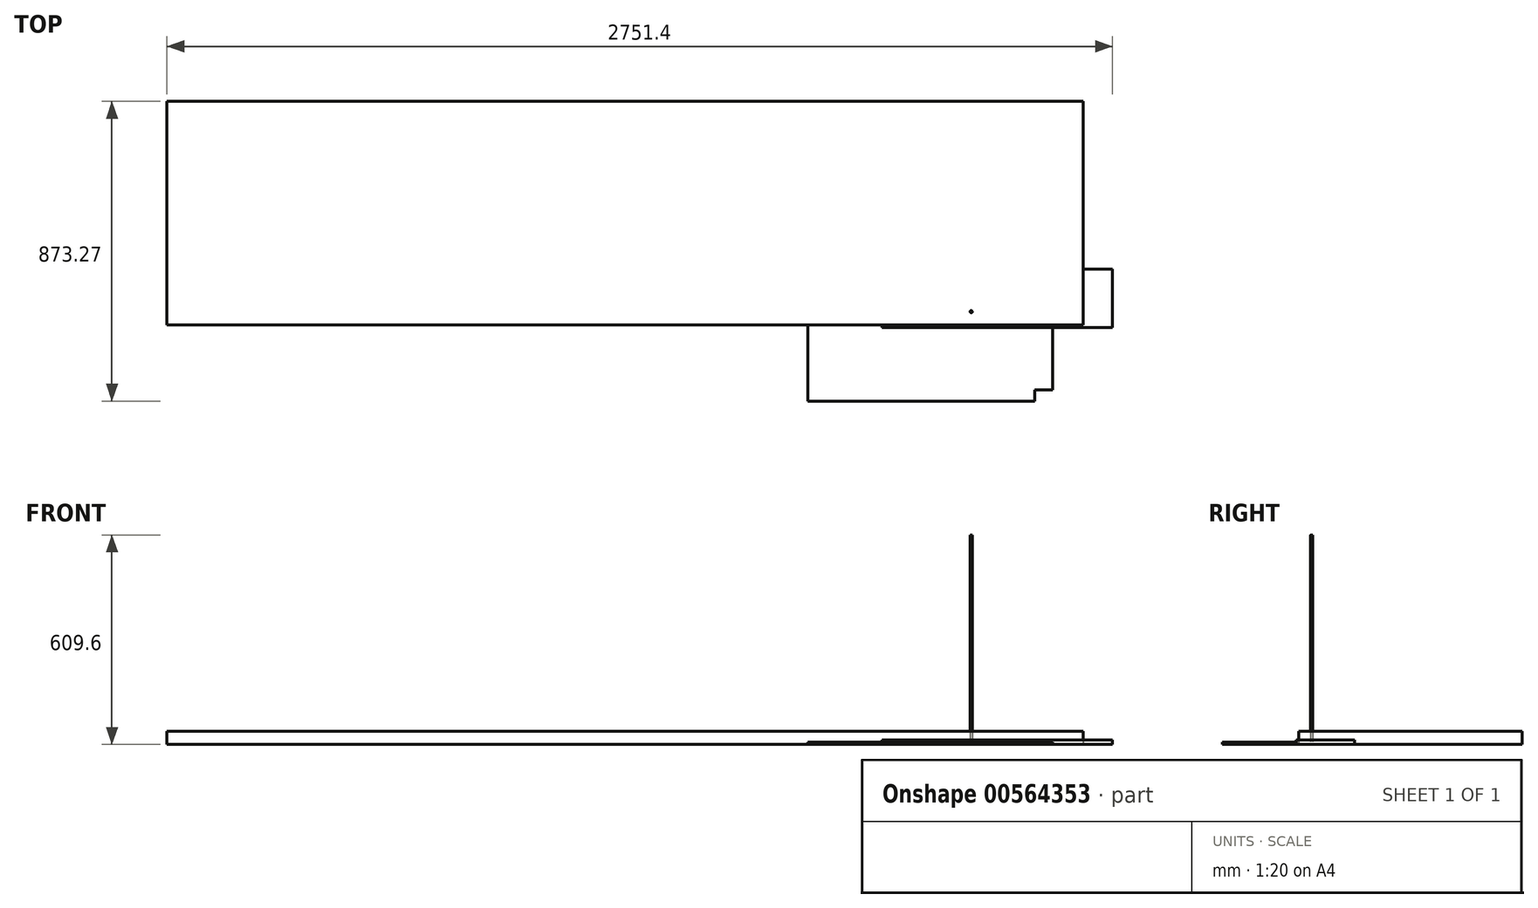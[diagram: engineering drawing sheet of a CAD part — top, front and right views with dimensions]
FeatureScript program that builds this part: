
annotation { "Feature Type Name" : "Feature", "Feature Type Description" : "" }
export const myFeature = defineFeature(function(context is Context, id is Id, definition is map)
    precondition{}
    {
        {
            var Q0;
            Q0=qCreatedBy(makeId("Top.planeOp"),FACE);
            var sketch = newSketch(context, id + "F0", { "sketchPlane" : qUnion([Q0])});
            skLineSegment(sketch, "E0.bottom", {"start": v(-2407.4, 611.97) * mm, "end": v(81.8, 611.97) * mm});
            skLineSegment(sketch, "E0.top", {"start": v(-2407.4, -38.9) * mm, "end": v(81.8, -38.9) * mm});
            skLineSegment(sketch, "E0.left", {"start": v(-2407.4, 611.97) * mm, "end": v(-2407.4, -38.9) * mm});
            skLineSegment(sketch, "E0.right", {"start": v(81.8, 611.97) * mm, "end": v(81.8, -38.9) * mm});
            skSolve(sketch);
        }
        {
            var Q0;
            Q0=makeQuery(id+"F0.imprint","IMPRINT",FACE,{"disambiguationData":[TD([[makeQuery(id+"F0.imprint","IMPRINT",EDGE,{"derivedFrom":sQuery(id+"F0.wireOp",EDGE,"E0.bottom")}),-1.0]])]});
            extrude(context, id + "F1", {"entities" : qUnion([Q0]), "depth" : 38.1 * mm, "offsetDistance" : 25.4 * mm});
        }
        {
            var Q0;
            Q0=qCreatedBy(makeId("Top.planeOp"),FACE);
            var sketch = newSketch(context, id + "F2", { "sketchPlane" : qUnion([Q0])});
            skLineSegment(sketch, "E1.bottom", {"start": v(-331.11, 48.4) * mm, "end": v(100.69, 48.4) * mm});
            skLineSegment(sketch, "E1.top", {"start": v(-331.11, -15.1) * mm, "end": v(100.69, -15.1) * mm});
            skLineSegment(sketch, "E1.left", {"start": v(-331.11, 48.4) * mm, "end": v(-331.11, -15.1) * mm});
            skLineSegment(sketch, "E1.right", {"start": v(100.69, 48.4) * mm, "end": v(100.69, -15.1) * mm});
            skSolve(sketch);
        }
        {
            var Q0;
            Q0=makeQuery(id+"F2.imprint","IMPRINT",FACE,{"disambiguationData":[TD([[makeQuery(id+"F2.imprint","IMPRINT",EDGE,{"derivedFrom":sQuery(id+"F2.wireOp",EDGE,"E1.bottom")}),-1.0]])]});
            extrude(context, id + "F3", {"entities" : qUnion([Q0]), "depth" : 12.7 * mm, "offsetDistance" : 25.4 * mm});
        }
        {
            var Q0;
            Q0=qCreatedBy(makeId("Top.planeOp"),FACE);
            var sketch = newSketch(context, id + "F4", { "sketchPlane" : qUnion([Q0])});
            skLineSegment(sketch, "E2.bottom", {"start": v(-326.55, 123.75) * mm, "end": v(166.2, 123.75) * mm});
            skLineSegment(sketch, "E2.top", {"start": v(-326.55, -46.43) * mm, "end": v(166.2, -46.43) * mm});
            skLineSegment(sketch, "E2.left", {"start": v(-326.55, 123.75) * mm, "end": v(-326.55, -46.43) * mm});
            skLineSegment(sketch, "E2.right", {"start": v(166.2, 123.75) * mm, "end": v(166.2, -46.43) * mm});
            skSolve(sketch);
        }
        {
            var Q0;
            Q0=makeQuery(id+"F4.imprint","IMPRINT",FACE,{"disambiguationData":[TD([[makeQuery(id+"F4.imprint","IMPRINT",EDGE,{"derivedFrom":sQuery(id+"F4.wireOp",EDGE,"E2.bottom")}),-1.0]])]});
            extrude(context, id + "F5", {"entities" : qUnion([Q0]), "depth" : 12.7 * mm, "offsetDistance" : 25.4 * mm});
        }
        {
            var Q0;
            Q0=qCreatedBy(makeId("Top.planeOp"),FACE);
            var sketch = newSketch(context, id + "F6", { "sketchPlane" : qUnion([Q0])});
            skLineSegment(sketch, "E3.bottom", {"start": v(-414.47, 393.37) * mm, "end": v(169.73, 393.37) * mm});
            skLineSegment(sketch, "E3.top", {"start": v(-414.47, -51.13) * mm, "end": v(169.73, -51.13) * mm});
            skLineSegment(sketch, "E3.left", {"start": v(-414.47, 393.37) * mm, "end": v(-414.47, -51.13) * mm});
            skLineSegment(sketch, "E3.right", {"start": v(169.73, 393.37) * mm, "end": v(169.73, -51.13) * mm});
            skSolve(sketch);
        }
        {
            var Q0;
            Q0=makeQuery(id+"F6.imprint","IMPRINT",FACE,{"disambiguationData":[TD([[makeQuery(id+"F6.imprint","IMPRINT",EDGE,{"derivedFrom":sQuery(id+"F6.wireOp",EDGE,"E3.bottom")}),-1.0]])]});
            extrude(context, id + "F7", {"entities" : qUnion([Q0]), "depth" : 6.35 * mm, "offsetDistance" : 25.4 * mm});
        }
        {
            var Q0;
            Q0=qCreatedBy(makeId("Top.planeOp"),FACE);
            var sketch = newSketch(context, id + "F8", { "sketchPlane" : qUnion([Q0])});
            skLineSegment(sketch, "E4.bottom", {"start": v(-542.59, 361) * mm, "end": v(117.81, 361) * mm});
            skLineSegment(sketch, "E4.top", {"start": v(-542.59, -83.5) * mm, "end": v(117.81, -83.5) * mm});
            skLineSegment(sketch, "E4.left", {"start": v(-542.59, 361) * mm, "end": v(-542.59, -83.5) * mm});
            skLineSegment(sketch, "E4.right", {"start": v(117.81, 361) * mm, "end": v(117.81, -83.5) * mm});
            skSolve(sketch);
        }
        {
            var Q0;
            Q0=makeQuery(id+"F8.imprint","IMPRINT",FACE,{"disambiguationData":[TD([[makeQuery(id+"F8.imprint","IMPRINT",EDGE,{"derivedFrom":sQuery(id+"F8.wireOp",EDGE,"E4.bottom")}),-1.0]])]});
            extrude(context, id + "F9", {"entities" : qUnion([Q0]), "depth" : 6.35 * mm, "offsetDistance" : 25.4 * mm});
        }
        {
            var Q0;
            Q0=qCreatedBy(makeId("Top.planeOp"),FACE);
            var sketch = newSketch(context, id + "F10", { "sketchPlane" : qUnion([Q0])});
            skCircle(sketch, "E5", {"center": v(-66.99, -0.84) * mm, "radius": 3.18 * mm});
            skSolve(sketch);
        }
        {
            var Q0;
            Q0=makeQuery(id+"F10.imprint","IMPRINT",FACE,{"disambiguationData":[TD([[makeQuery(id+"F10.imprint","IMPRINT",EDGE,{"derivedFrom":sQuery(id+"F10.wireOp",EDGE,"E5")}),1.0]])]});
            extrude(context, id + "F11", {"entities" : qUnion([Q0]), "depth" : 609.6 * mm, "offsetDistance" : 25.4 * mm});
        }
        {
            var Q0;
            Q0=makeQuery(id+"F9.opExtrude","SWEPT_FACE",FACE,{"disambiguationData":[OSD([sQuery(id+"F8.wireOp",EDGE,"E4.top")])]});
            extrude(context, id + "F12", {"entities" : qUnion([Q0]), "operationType" : NewBodyOperationType.ADD, "depth" : 177.8 * mm, "offsetDistance" : 25.4 * mm});
        }
        {
            var Q0;
            Q0=makeQuery(id+"F7.opExtrude","SWEPT_FACE",FACE,{"disambiguationData":[OSD([sQuery(id+"F6.wireOp",EDGE,"E3.top")])]});
            extrude(context, id + "F13", {"entities" : qUnion([Q0]), "operationType" : NewBodyOperationType.ADD, "depth" : 177.8 * mm, "offsetDistance" : 25.4 * mm});
        }
        {
            var Q0;
            Q0=makeQuery(id+"F5.opExtrude","SWEPT_FACE",FACE,{"disambiguationData":[OSD([sQuery(id+"F4.wireOp",EDGE,"E2.right")])]});
            extrude(context, id + "F14", {"entities" : qUnion([Q0]), "operationType" : NewBodyOperationType.ADD, "depth" : 177.8 * mm, "offsetDistance" : 25.4 * mm});
        }
        {
            var Q0;
            Q0=makeQuery(id+"F3.opExtrude","SWEPT_FACE",FACE,{"disambiguationData":[OSD([sQuery(id+"F2.wireOp",EDGE,"E1.right")])]});
            extrude(context, id + "F15", {"entities" : qUnion([Q0]), "operationType" : NewBodyOperationType.ADD, "depth" : 177.8 * mm, "offsetDistance" : 25.4 * mm});
        }
        {
            var Q0;
            Q0=makeQuery(id+"F1.opExtrude","SWEPT_FACE",FACE,{"disambiguationData":[OSD([sQuery(id+"F0.wireOp",EDGE,"E0.right")])]});
            extrude(context, id + "F16", {"entities" : qUnion([Q0]), "operationType" : NewBodyOperationType.ADD, "depth" : 177.8 * mm, "offsetDistance" : 25.4 * mm});
        }
    });
